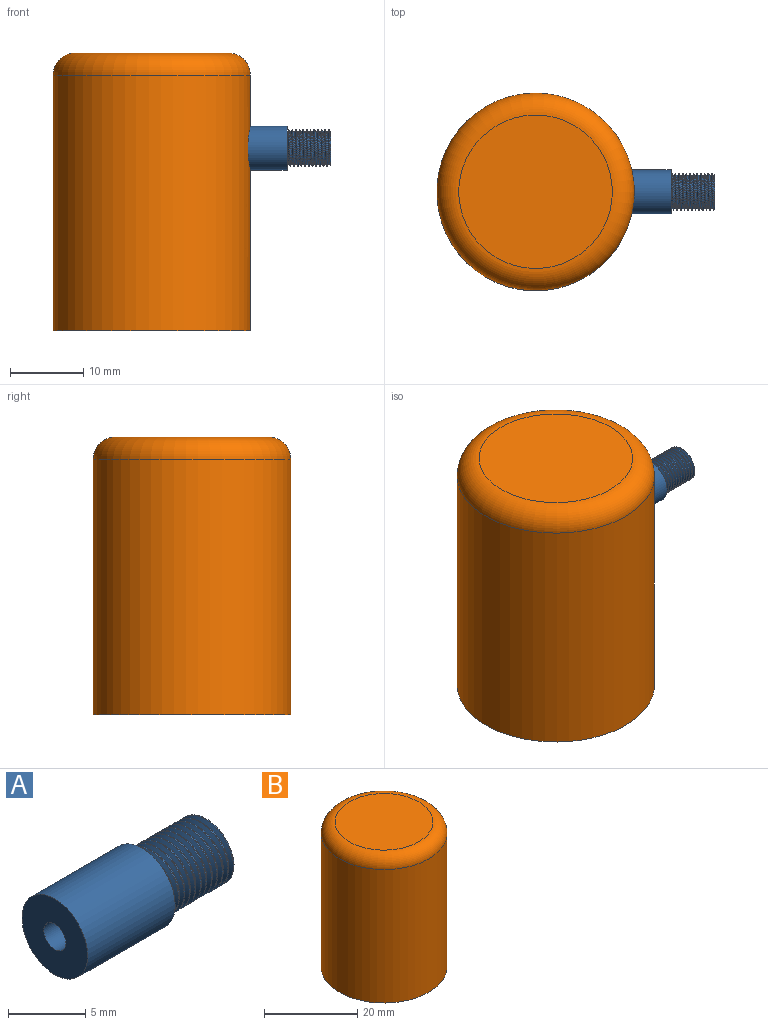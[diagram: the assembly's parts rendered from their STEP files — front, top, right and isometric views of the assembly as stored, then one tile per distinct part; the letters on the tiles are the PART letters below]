
ASSEMBLY  parts=2 mates=1
PART A: 10 faces, bbox 14.3x6.1x6.1 mm
  f0: plane 4.52x4.48mm, normal (1,0,0), area 12.6mm2, adj f4,f6,f7,f8,f9
  f1: cylinder r=2.5mm len=5.88mm, axis (1,0,0), area 10.6mm2, adj f5,f7,f8,f9
  f2: cylinder r=3mm len=8mm, axis (1,0,0), area 150.8mm2, adj f3,f5
  f3: plane 6x6mm, normal (-1,0,0), area 25.1mm2, adj f2,f4
  f4: cylinder r=1mm len=14mm, axis (1,0,0), area 88mm2, adj f0,f3
  f5: plane 6.14x6.14mm, normal (1,0,0), area 11mm2, adj f1,f2,f6,f7,f8
  f6: bspline ~6.38x5.15mm, area 23.3mm2, adj f0,f5,f7,f8
  f7: bspline ~6.41x5.77mm, area 55.1mm2, adj f0,f1,f5,f6,f9
  f8: bspline ~6.24x5.77mm, area 55.3mm2, adj f0,f1,f5,f6,f9
  f9: cone r=2.5mm half-angle=63.4deg, axis (-1,0,0), area 1.7mm2, adj f0,f1,f7,f8
PART B: 14 faces, bbox 29.2x29.2x38 mm
  f0: cylinder r=13.5mm len=35mm, axis (0,0,-1), area 2940.4mm2, adj f4,f5,f13
  f1: cylinder r=3.5mm len=32mm, axis (0,0,-1), area 658.5mm2, adj f4,f7,f12,f13
  f2: cylinder r=6mm len=27mm, axis (0,0,-1), area 1005.1mm2, adj f4,f6,f12
  f3: plane 21x21mm, normal (0,0,1), area 346.4mm2, adj f5
  f4: plane 27x27mm, normal (0,0,-1), area 411.2mm2, adj f0,f1,f2,f9,f11
  f5: torus R=10.5mm, axis (0,0,1), area 367.4mm2, adj f0,f3
  f6: plane 12x12mm, normal (0,0,-1), area 113.1mm2, adj f2
  f7: plane 7x7mm, normal (0,0,-1), area 38.5mm2, adj f1
  f8: cone r=0mm half-angle=59deg, axis (0,0,-1), area 5.7mm2, adj f9
  f9: cylinder r=1.25mm len=8mm, axis (0,0,-1), area 62.8mm2, adj f4,f8
  f10: cone r=0mm half-angle=59deg, axis (0,0,-1), area 5.7mm2, adj f11
  f11: cylinder r=1.25mm len=8mm, axis (0,0,-1), area 62.8mm2, adj f4,f10
  f12: cylinder r=2mm len=4.47mm, axis (1,0,0), area 50mm2, adj f1,f2
  f13: cylinder r=3mm len=6mm, axis (1,0,0), area 68.1mm2, adj f0,f1
PLACE A t=(0.03,0,0)mm
PLACE B at identity fixed
MATE fastened A.f1 <-> B.f12  axis (1,0,0) through (10.53,0,25)mm
